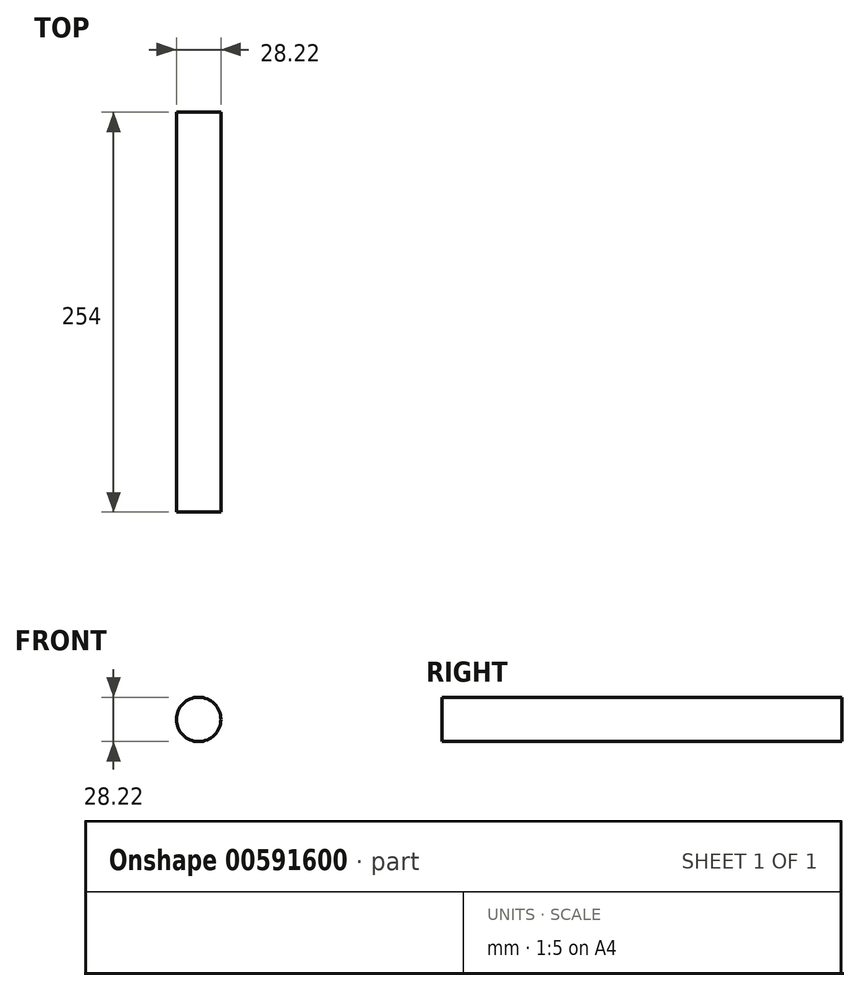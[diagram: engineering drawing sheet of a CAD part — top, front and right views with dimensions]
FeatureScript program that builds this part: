
annotation { "Feature Type Name" : "Feature", "Feature Type Description" : "" }
export const myFeature = defineFeature(function(context is Context, id is Id, definition is map)
    precondition{}
    {
        {
            var Q0;
            Q0=qCreatedBy(makeId("Front.planeOp"),FACE);
            var sketch = newSketch(context, id + "F0", { "sketchPlane" : qUnion([Q0])});
            skCircle(sketch, "E0", {"center": v(0, 0) * mm, "radius": 14.1 * mm});
            skSolve(sketch);
        }
        {
            var Q0;
            Q0=makeQuery(id+"F0.imprint","IMPRINT",FACE,{"disambiguationData":[TD([[makeQuery(id+"F0.imprint","IMPRINT",EDGE,{"derivedFrom":sQuery(id+"F0.wireOp",EDGE,"E0")}),1.0]])]});
            extrude(context, id + "F1", {"entities" : qUnion([Q0]), "depth" : 254 * mm, "offsetDistance" : 25.4 * mm});
        }
    });
